FCSTD DOCUMENT  (FreeCAD 0.19R24276 (Git))
Label: Assambly_2
License: All rights reserved
LicenseURL: http://en.wikipedia.org/wiki/All_rights_reserved
objects: App::DocumentObjectGroup×3, PartDesign::CoordinateSystem×3, PartDesign::Body×1, Sketcher::SketchObject×1, App::FeaturePython×1, App::Part×1
note: 5 computed .brp shape members not serialized (recipe doc carries the construction recipe); baked Part::Feature solids carry a one-line shape summary decoded from their .brp

FEATURE [PartDesign::Body] Body  label="Master_sketch_M_body"
  Origin = -> Origin
FEATURE [Sketcher::SketchObject] Sketch  label="Master_sketch_M"
  FullyConstrained = false
  MapMode = 5
  Support = -> [XY_Plane001]
  sketch-geometry (5):
    g0: LineSegment StartX=27.3616 StartY=75.1754 StartZ=0 EndX=0 EndY=0 EndZ=0
    g1: LineSegment StartX=0 StartY=0 StartZ=0 EndX=-193.998 EndY=157.685 EndZ=0
    g2: LineSegment StartX=27.3616 StartY=75.1754 StartZ=0 EndX=-166.637 EndY=232.861 EndZ=0
    g3: LineSegment StartX=-193.998 StartY=157.685 StartZ=0 EndX=-166.637 EndY=232.861 EndZ=0
    g4: LineSegment StartX=-193.998 StartY=157.685 StartZ=0 EndX=-279.503 EndY=-77.2379 EndZ=0
  constraints (13):
    c: Coincident(g1,g0)
    c: Distance(g1) = 250
    c: Distance(g0) = 80
    c: Coincident(g0,g2)
    c: Coincident(g0,g-1)
    c: Coincident(g3,g1)
    c: Distance(g3) = 80
    c: Coincident(g4,g1)
    c: Parallel(g3,g4)
    c: Coincident(g3,g2)
    c: Distance(g1,g4) = 250
    c: Equal(g1,g2)
    c: Angle(g-1,g0) = 1.22173
FEATURE [App::DocumentObjectGroup] Parts
  Group = -> [Body]
FEATURE [PartDesign::CoordinateSystem] LCS_Origin
  AttacherType = Attacher::AttachEngine3D
  MapMode = 2
  Support = -> [X_Axis001]
FEATURE [App::FeaturePython] Variables  # WARN: FeaturePython — macro-defined, semantics opaque (R4)
  Ax1 = 141
  Ax2 = 62
  Type = App::PropertyContainer
FEATURE [App::DocumentObjectGroup] Constraints
  Group = -> [Sketch]
FEATURE [App::DocumentObjectGroup] Configurations
FEATURE [PartDesign::CoordinateSystem] LCS_Ax1
  AttacherType = Attacher::AttachEngine3D
  MapMode = 51
  Placement = pos=(-193.998,157.685,0) rot=(0,0,1;0.888288rad)
  Support = -> [Sketch]
FEATURE [PartDesign::CoordinateSystem] LCS_AX_2  label="LCS_Ax2"
  AttacherType = Attacher::AttachEngine3D
  MapMode = 49
  Placement = pos=(27.3616,75.1754,0) rot=(0,0,-1;1.91986rad)
  Support = -> [Sketch]
FEATURE [App::Part] Assembly
  AssemblyType = Part::Link
  Group = -> [LCS_Origin,Variables,Constraints,Configurations,Sketch,LCS_Ax1,LCS_AX_2]
  Origin = -> Origin001
  Type = Assembly
